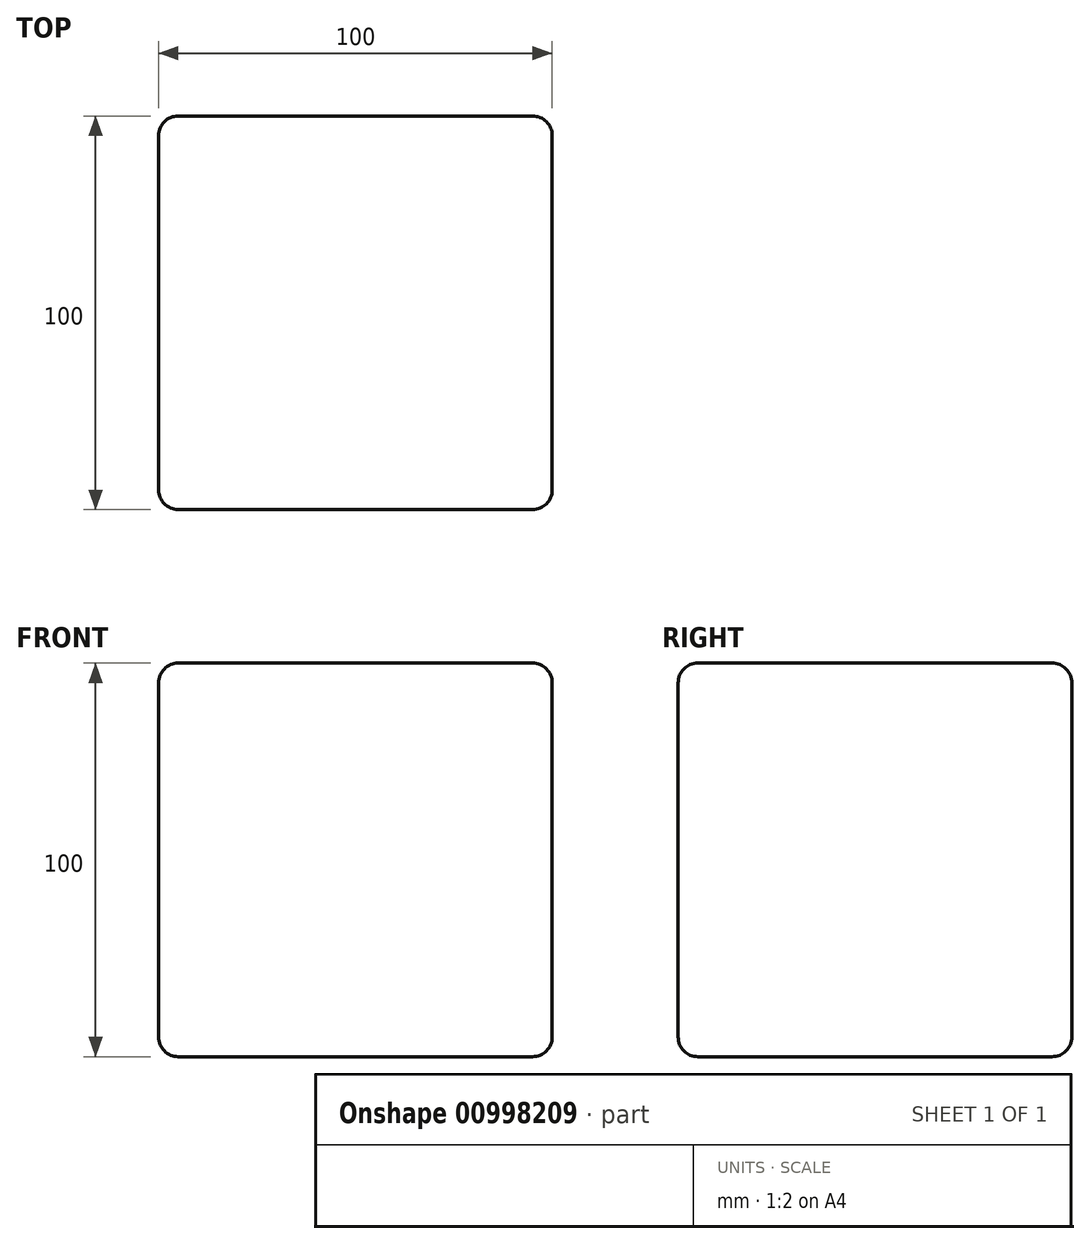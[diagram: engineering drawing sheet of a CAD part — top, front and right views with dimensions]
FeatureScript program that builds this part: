
annotation { "Feature Type Name" : "Feature", "Feature Type Description" : "" }
export const myFeature = defineFeature(function(context is Context, id is Id, definition is map)
    precondition{}
    {
        {
            var Q0;
            Q0=qCreatedBy(makeId("Front.planeOp"),FACE);
            var sketch = newSketch(context, id + "F0", { "sketchPlane" : qUnion([Q0])});
            skLineSegment(sketch, "E0.bottom", {"start": v(0, 0) * mm, "end": v(100, 0) * mm});
            skLineSegment(sketch, "E0.top", {"start": v(0, 100) * mm, "end": v(100, 100) * mm});
            skLineSegment(sketch, "E0.left", {"start": v(0, 0) * mm, "end": v(0, 100) * mm});
            skLineSegment(sketch, "E0.right", {"start": v(100, 0) * mm, "end": v(100, 100) * mm});
            skSolve(sketch);
        }
        {
            var Q0;
            Q0=makeQuery(id+"F0.imprint","IMPRINT",FACE,{"disambiguationData":[TD([[makeQuery(id+"F0.imprint","IMPRINT",EDGE,{"derivedFrom":sQuery(id+"F0.wireOp",EDGE,"E0.bottom")}),1.0]])]});
            extrude(context, id + "F1", {"entities" : qUnion([Q0]), "depth" : 100 * mm, "offsetDistance" : 25 * mm});
        }
        {
            var Q0;
            Q0=makeQuery(id+"F1.opExtrude","SWEPT_EDGE",EDGE,{"disambiguationData":[OSD([sQuery(id+"F0.wireOp",EDGE,"E0.top"),sQuery(id+"F0.wireOp",EDGE,"E0.left")])]});
            var Q1;
            Q1=makeQuery(id+"F1.opExtrude","CAP_EDGE",EDGE,{"disambiguationData":[OSD([sQuery(id+"F0.wireOp",EDGE,"E0.top")])],"isStart":false});
            var Q2;
            Q2=makeQuery(id+"F1.opExtrude","SWEPT_EDGE",EDGE,{"disambiguationData":[OSD([sQuery(id+"F0.wireOp",EDGE,"E0.top"),sQuery(id+"F0.wireOp",EDGE,"E0.right")])]});
            var Q3;
            Q3=makeQuery(id+"F1.opExtrude","CAP_EDGE",EDGE,{"disambiguationData":[OSD([sQuery(id+"F0.wireOp",EDGE,"E0.top")])],"isStart":true});
            var Q4;
            Q4=makeQuery(id+"F1.opExtrude","CAP_EDGE",EDGE,{"disambiguationData":[OSD([sQuery(id+"F0.wireOp",EDGE,"E0.right")])],"isStart":true});
            var Q5;
            Q5=makeQuery(id+"F1.opExtrude","CAP_EDGE",EDGE,{"disambiguationData":[OSD([sQuery(id+"F0.wireOp",EDGE,"E0.right")])],"isStart":false});
            var Q6;
            Q6=makeQuery(id+"F1.opExtrude","CAP_EDGE",EDGE,{"disambiguationData":[OSD([sQuery(id+"F0.wireOp",EDGE,"E0.left")])],"isStart":false});
            var Q7;
            Q7=makeQuery(id+"F1.opExtrude","CAP_EDGE",EDGE,{"disambiguationData":[OSD([sQuery(id+"F0.wireOp",EDGE,"E0.bottom")])],"isStart":false});
            var Q8;
            Q8=makeQuery(id+"F1.opExtrude","SWEPT_EDGE",EDGE,{"disambiguationData":[OSD([sQuery(id+"F0.wireOp",EDGE,"E0.bottom"),sQuery(id+"F0.wireOp",EDGE,"E0.right")])]});
            var Q9;
            Q9=makeQuery(id+"F1.opExtrude","SWEPT_EDGE",EDGE,{"disambiguationData":[OSD([sQuery(id+"F0.wireOp",EDGE,"E0.bottom"),sQuery(id+"F0.wireOp",EDGE,"E0.left")])]});
            var Q10;
            Q10=makeQuery(id+"F1.opExtrude","CAP_EDGE",EDGE,{"disambiguationData":[OSD([sQuery(id+"F0.wireOp",EDGE,"E0.bottom")])],"isStart":true});
            var Q11;
            Q11=makeQuery(id+"F1.opExtrude","CAP_EDGE",EDGE,{"disambiguationData":[OSD([sQuery(id+"F0.wireOp",EDGE,"E0.left")])],"isStart":true});
            fillet(context, id + "F2", {"entities" : qUnion([Q0, Q1, Q2, Q3, Q4, Q5, Q6, Q7, Q8, Q9, Q10, Q11]), "radius" : 5 * mm, "tangentPropagation" : true, "allowEdgeOverflow" : false});
        }
    });
